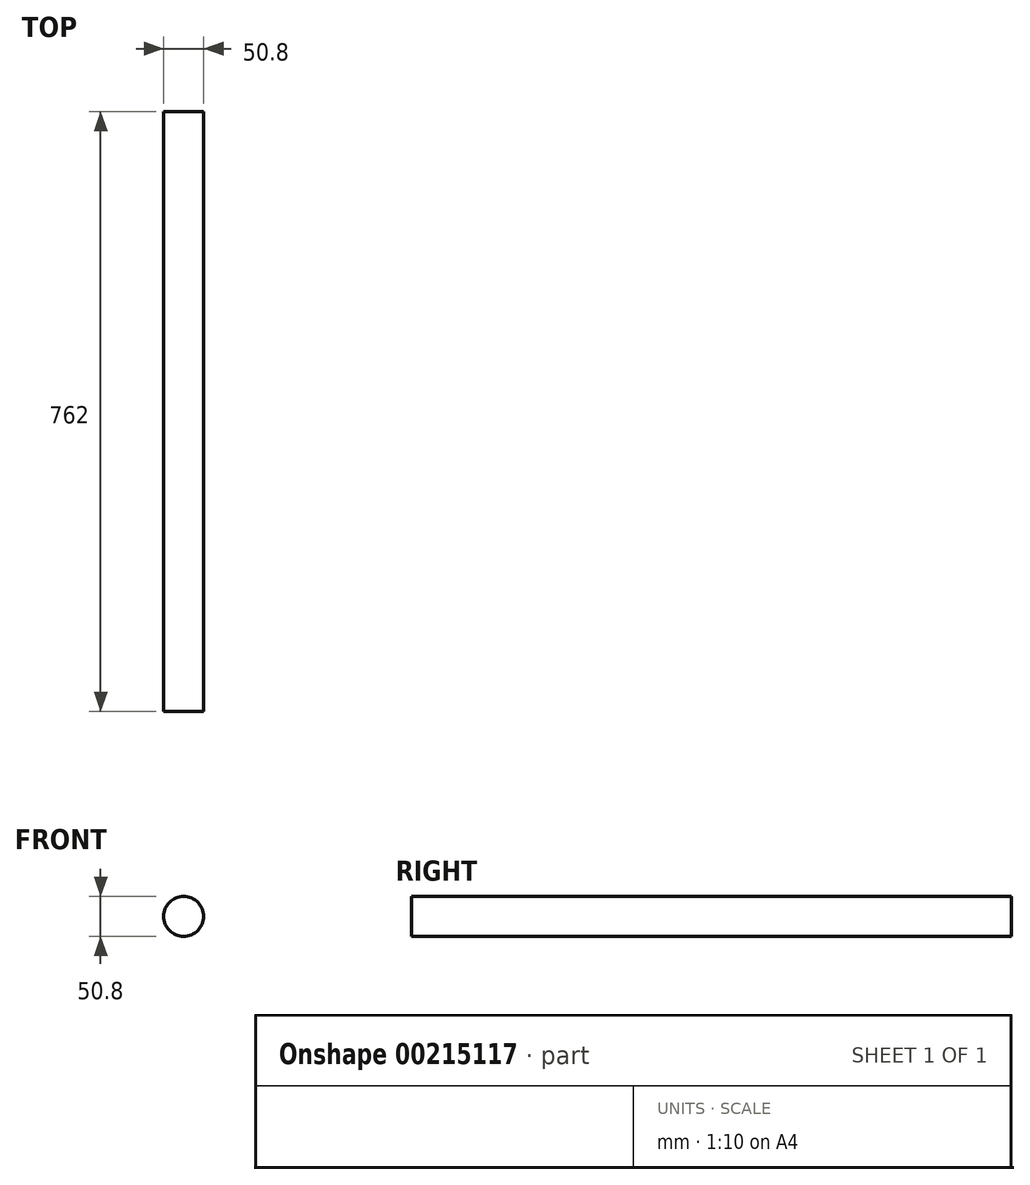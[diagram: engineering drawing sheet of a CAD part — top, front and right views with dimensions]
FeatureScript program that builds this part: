
annotation { "Feature Type Name" : "Feature", "Feature Type Description" : "" }
export const myFeature = defineFeature(function(context is Context, id is Id, definition is map)
    precondition{}
    {
        {
            var Q0;
            Q0=qCreatedBy(makeId("Front.planeOp"),FACE);
            var sketch = newSketch(context, id + "F0", { "sketchPlane" : qUnion([Q0])});
            skCircle(sketch, "E0", {"center": v(0, 0) * mm, "radius": 25.4 * mm});
            skSolve(sketch);
        }
        {
            var Q0;
            Q0 = qSketchRegion(id + "F0", true);
            extrude(context, id + "F1", {"entities" : qUnion([Q0]), "depth" : 762 * mm});
        }
    });
